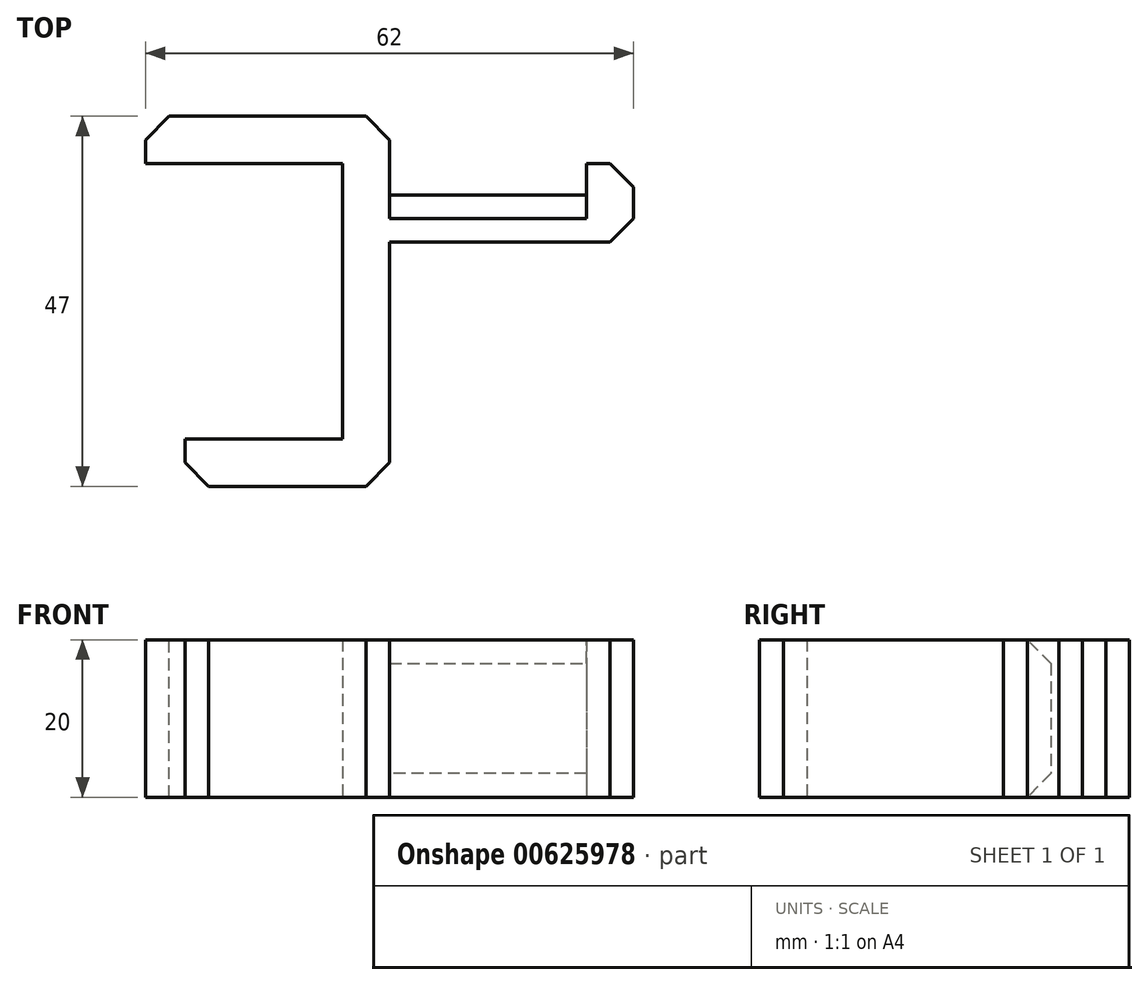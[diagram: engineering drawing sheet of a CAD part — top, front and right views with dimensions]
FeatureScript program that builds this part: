
annotation { "Feature Type Name" : "Feature", "Feature Type Description" : "" }
export const myFeature = defineFeature(function(context is Context, id is Id, definition is map)
    precondition{}
    {
        {
            var Q0;
            Q0=qCreatedBy(makeId("Top.planeOp"),FACE);
            var sketch = newSketch(context, id + "F0", { "sketchPlane" : qUnion([Q0])});
            skLineSegment(sketch, "E0", {"start": v(-25, 0) * mm, "end": v(0, 0) * mm});
            skLineSegment(sketch, "E1", {"start": v(0, 0) * mm, "end": v(0, -35) * mm});
            skLineSegment(sketch, "E2", {"start": v(0, -35) * mm, "end": v(-20, -35) * mm});
            skLineSegment(sketch, "E3", {"start": v(-20, -35) * mm, "end": v(-20, -41) * mm});
            skLineSegment(sketch, "E4", {"start": v(-20, -41) * mm, "end": v(6, -41) * mm});
            skLineSegment(sketch, "E5", {"start": v(6, -41) * mm, "end": v(6, -10) * mm});
            skLineSegment(sketch, "E6", {"start": v(6, -10) * mm, "end": v(37, -10) * mm});
            skLineSegment(sketch, "E7", {"start": v(37, -10) * mm, "end": v(37, 0) * mm});
            skLineSegment(sketch, "E8", {"start": v(37, 0) * mm, "end": v(31, 0) * mm});
            skLineSegment(sketch, "E9", {"start": v(31, 0) * mm, "end": v(31, -4) * mm});
            skLineSegment(sketch, "E10", {"start": v(31, -4) * mm, "end": v(6, -4) * mm});
            skLineSegment(sketch, "E11", {"start": v(6, -4) * mm, "end": v(6, 6) * mm});
            skLineSegment(sketch, "E12", {"start": v(6, 6) * mm, "end": v(-25, 6) * mm});
            skLineSegment(sketch, "E13", {"start": v(-25, 6) * mm, "end": v(-25, 0) * mm});
            skSolve(sketch);
        }
        {
            var Q0;
            Q0 = qSketchRegion(id + "F0", true);
            extrude(context, id + "F1", {"entities" : qUnion([Q0]), "depth" : 20 * mm, "offsetDistance" : 25 * mm});
        }
        {
            var Q0;
            Q0=makeQuery(id+"F1.opExtrude","SWEPT_EDGE",EDGE,{"disambiguationData":[OSD([sQuery(id+"F0.wireOp",EDGE,"E6"),sQuery(id+"F0.wireOp",EDGE,"E7")])]});
            var Q1;
            Q1=makeQuery(id+"F1.opExtrude","SWEPT_EDGE",EDGE,{"disambiguationData":[OSD([sQuery(id+"F0.wireOp",EDGE,"E11"),sQuery(id+"F0.wireOp",EDGE,"E12")])]});
            var Q2;
            Q2=makeQuery(id+"F1.opExtrude","SWEPT_EDGE",EDGE,{"disambiguationData":[OSD([sQuery(id+"F0.wireOp",EDGE,"E4"),sQuery(id+"F0.wireOp",EDGE,"E5")])]});
            var Q3;
            Q3=makeQuery(id+"F1.opExtrude","SWEPT_EDGE",EDGE,{"disambiguationData":[OSD([sQuery(id+"F0.wireOp",EDGE,"E12"),sQuery(id+"F0.wireOp",EDGE,"E13")])]});
            var Q4;
            Q4=makeQuery(id+"F1.opExtrude","SWEPT_EDGE",EDGE,{"disambiguationData":[OSD([sQuery(id+"F0.wireOp",EDGE,"E3"),sQuery(id+"F0.wireOp",EDGE,"E4")])]});
            var Q5;
            Q5=makeQuery(id+"F1.opExtrude","SWEPT_EDGE",EDGE,{"disambiguationData":[OSD([sQuery(id+"F0.wireOp",EDGE,"E7"),sQuery(id+"F0.wireOp",EDGE,"E8")])]});
            chamfer(context, id + "F2", {"entities" : qUnion([Q0, Q1, Q2, Q3, Q4, Q5]), "width" : 3 * mm, "tangentPropagation" : true});
        }
        {
            var Q0;
            Q0=makeQuery(id+"F1.opExtrude","CAP_EDGE",EDGE,{"disambiguationData":[OSD([sQuery(id+"F0.wireOp",EDGE,"E10")])],"isStart":false});
            var Q1;
            Q1=makeQuery(id+"F1.opExtrude","CAP_EDGE",EDGE,{"disambiguationData":[OSD([sQuery(id+"F0.wireOp",EDGE,"E10")])],"isStart":true});
            chamfer(context, id + "F3", {"entities" : qUnion([Q0, Q1]), "width" : 3 * mm, "tangentPropagation" : true});
        }
    });
